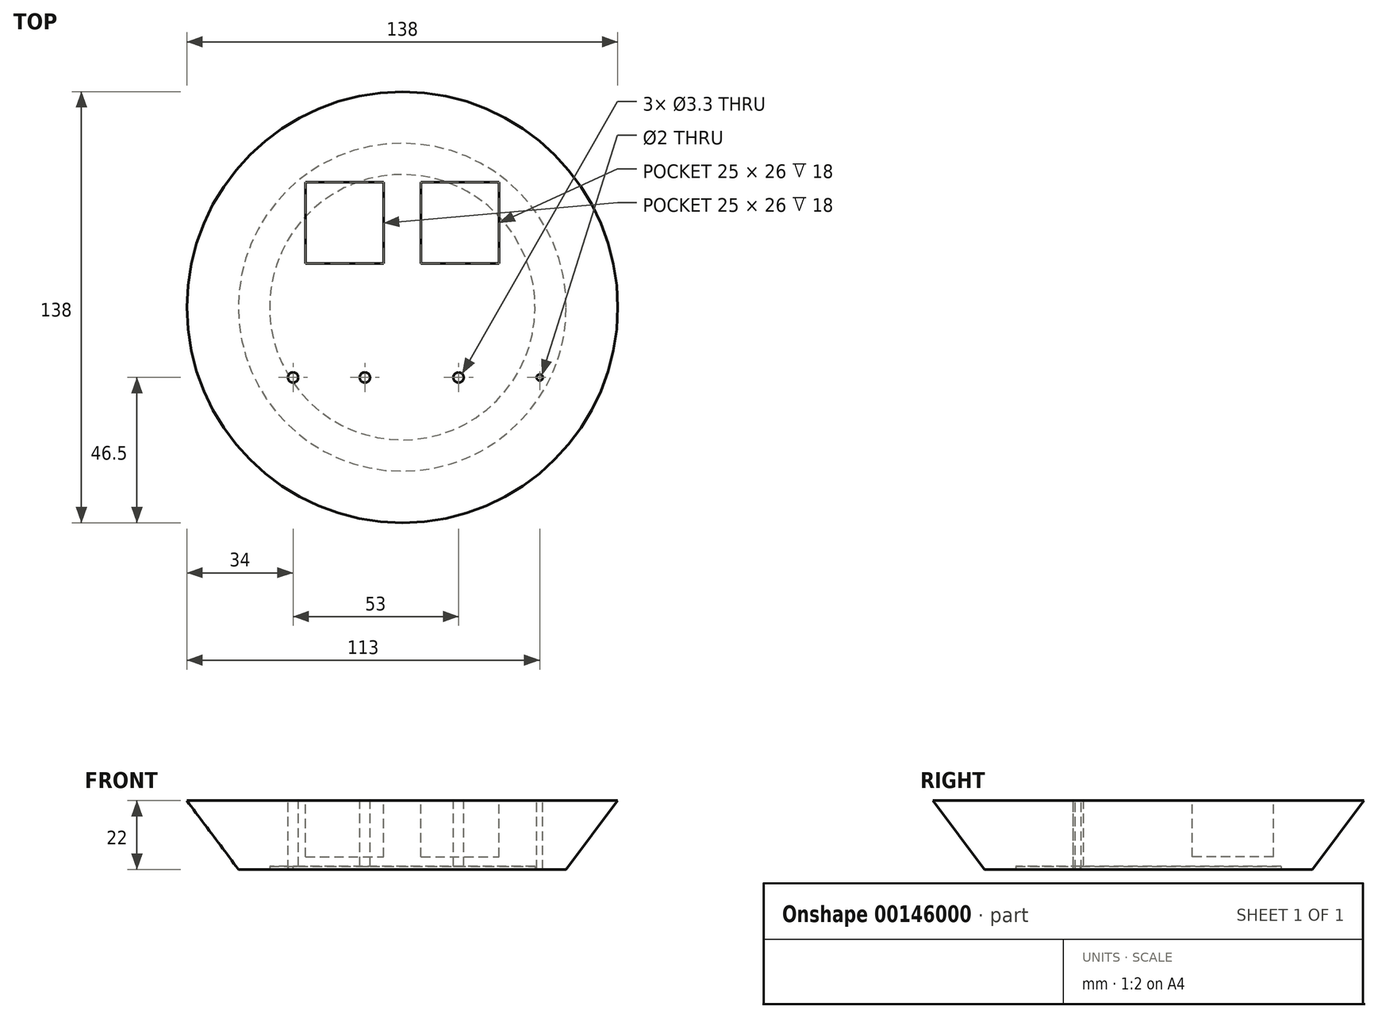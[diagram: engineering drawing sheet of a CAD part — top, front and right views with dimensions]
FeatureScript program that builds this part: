
annotation { "Feature Type Name" : "Feature", "Feature Type Description" : "" }
export const myFeature = defineFeature(function(context is Context, id is Id, definition is map)
    precondition{}
    {
        {
            var Q0;
            Q0=qCreatedBy(makeId("Front.planeOp"),FACE);
            var sketch = newSketch(context, id + "F0", { "sketchPlane" : qUnion([Q0])});
            skLineSegment(sketch, "E0", {"start": v(0, 1) * mm, "end": v(42.5, 1) * mm});
            skLineSegment(sketch, "E1", {"start": v(42.5, 1) * mm, "end": v(42.5, 0) * mm});
            skLineSegment(sketch, "E2", {"start": v(42.5, 0) * mm, "end": v(52.5, 0) * mm});
            skLineSegment(sketch, "E3", {"start": v(0, 1) * mm, "end": v(0, 22) * mm});
            skLineSegment(sketch, "E4", {"start": v(0, 22) * mm, "end": v(69, 22) * mm});
            skLineSegment(sketch, "E5", {"start": v(69, 22) * mm, "end": v(52.5, 0) * mm});
            skSolve(sketch);
        }
        {
            var Q0;
            Q0=makeQuery(id+"F0.imprint","IMPRINT",FACE,{"disambiguationData":[TD([[makeQuery(id+"F0.imprint","IMPRINT",EDGE,{"derivedFrom":sQuery(id+"F0.wireOp",EDGE,"E0")}),1.0]])]});
            var Q1;
            Q1=sQuery(id+"F0.wireOp",EDGE,"E3");
            revolve(context, id + "F1", {"entities" : qUnion([Q0]), "axis" : qUnion([Q1]), "revolveType" : RevolveType.FULL});
        }
        {
            var Q0;
            Q0=makeQuery(id+"F1.opRevolve","SWEPT_FACE",FACE,{"disambiguationData":[OSD([sQuery(id+"F0.wireOp",EDGE,"E4")])]});
            var sketch = newSketch(context, id + "F2", { "sketchPlane" : qUnion([Q0])});
            skCircle(sketch, "E6", {"center": v(-35, -22.5) * mm, "radius": 1.65 * mm});
            skCircle(sketch, "E7", {"center": v(-12, -22.5) * mm, "radius": 1.65 * mm});
            skCircle(sketch, "E8", {"center": v(18, -22.5) * mm, "radius": 1.65 * mm});
            skCircle(sketch, "E9", {"center": v(44, -22.5) * mm, "radius": 1 * mm});
            skSolve(sketch);
        }
        {
            var Q0;
            Q0 = qSketchRegion(id + "F2", true);
            extrude(context, id + "F3", {"entities" : qUnion([Q0]), "operationType" : NewBodyOperationType.REMOVE, "oppositeDirection" : true, "depth" : 25 * mm});
        }
        {
            var Q0;
            Q0=makeQuery(id+"F1.opRevolve","SWEPT_FACE",FACE,{"disambiguationData":[OSD([sQuery(id+"F0.wireOp",EDGE,"E4")])]});
            var sketch = newSketch(context, id + "F4", { "sketchPlane" : qUnion([Q0])});
            skLineSegment(sketch, "E10", {"start": v(-6, 14) * mm, "end": v(-6, 40) * mm});
            skLineSegment(sketch, "E11", {"start": v(-6, 40) * mm, "end": v(-31, 40) * mm});
            skLineSegment(sketch, "E12", {"start": v(-31, 40) * mm, "end": v(-31, 14) * mm});
            skLineSegment(sketch, "E13", {"start": v(-31, 14) * mm, "end": v(-6, 14) * mm});
            skLineSegment(sketch, "E14", {"start": v(6, 14) * mm, "end": v(31, 14) * mm});
            skLineSegment(sketch, "E15", {"start": v(31, 14) * mm, "end": v(31, 40) * mm});
            skLineSegment(sketch, "E16", {"start": v(31, 40) * mm, "end": v(6, 40) * mm});
            skLineSegment(sketch, "E17", {"start": v(6, 40) * mm, "end": v(6, 14) * mm});
            skSolve(sketch);
        }
        {
            var Q0;
            Q0=makeQuery(id+"F4.imprint","IMPRINT",FACE,{"disambiguationData":[TD([[makeQuery(id+"F4.imprint","IMPRINT",EDGE,{"derivedFrom":sQuery(id+"F4.wireOp",EDGE,"E10")}),1.0]])]});
            var Q1;
            Q1=makeQuery(id+"F4.imprint","IMPRINT",FACE,{"disambiguationData":[TD([[makeQuery(id+"F4.imprint","IMPRINT",EDGE,{"derivedFrom":sQuery(id+"F4.wireOp",EDGE,"E14")}),1.0]])]});
            extrude(context, id + "F5", {"entities" : qUnion([Q0, Q1]), "operationType" : NewBodyOperationType.REMOVE, "oppositeDirection" : true, "depth" : 18 * mm});
        }
    });
